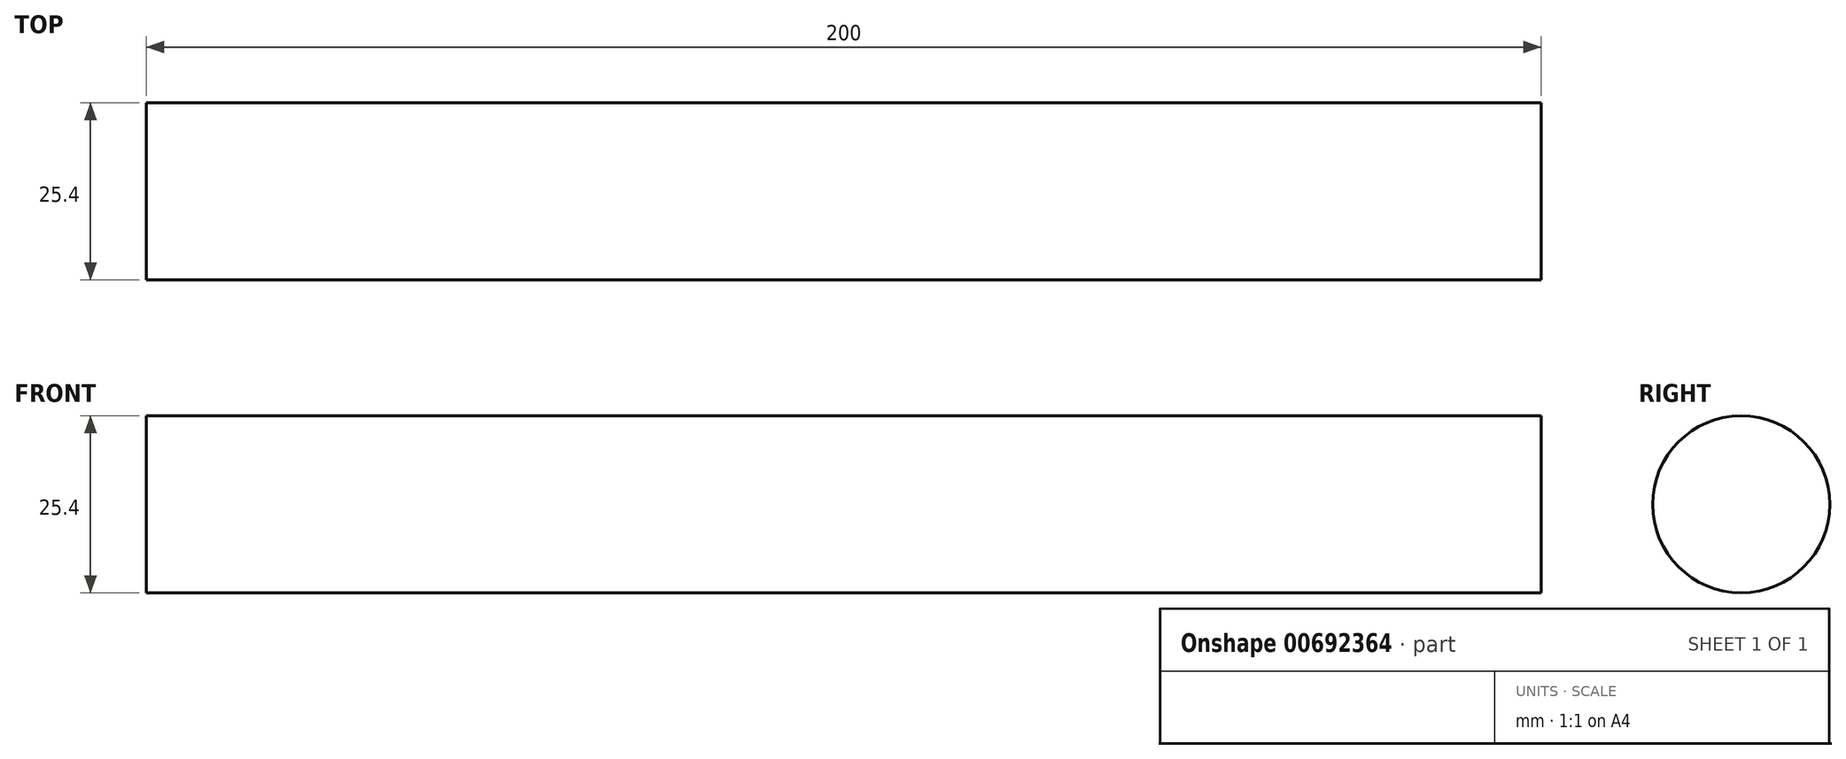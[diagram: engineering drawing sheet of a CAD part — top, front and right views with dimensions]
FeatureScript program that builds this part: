
annotation { "Feature Type Name" : "Feature", "Feature Type Description" : "" }
export const myFeature = defineFeature(function(context is Context, id is Id, definition is map)
    precondition{}
    {
        {
            var Q0;
            Q0=qCreatedBy(makeId("Right.planeOp"),FACE);
            var sketch = newSketch(context, id + "F0", { "sketchPlane" : qUnion([Q0])});
            skCircle(sketch, "E0", {"center": v(0, 0) * mm, "radius": 12.7 * mm});
            skSolve(sketch);
        }
        {
            var Q0;
            Q0 = qSketchRegion(id + "F0", true);
            extrude(context, id + "F1", {"entities" : qUnion([Q0]), "depth" : 200 * mm, "offsetDistance" : 25 * mm});
        }
    });
